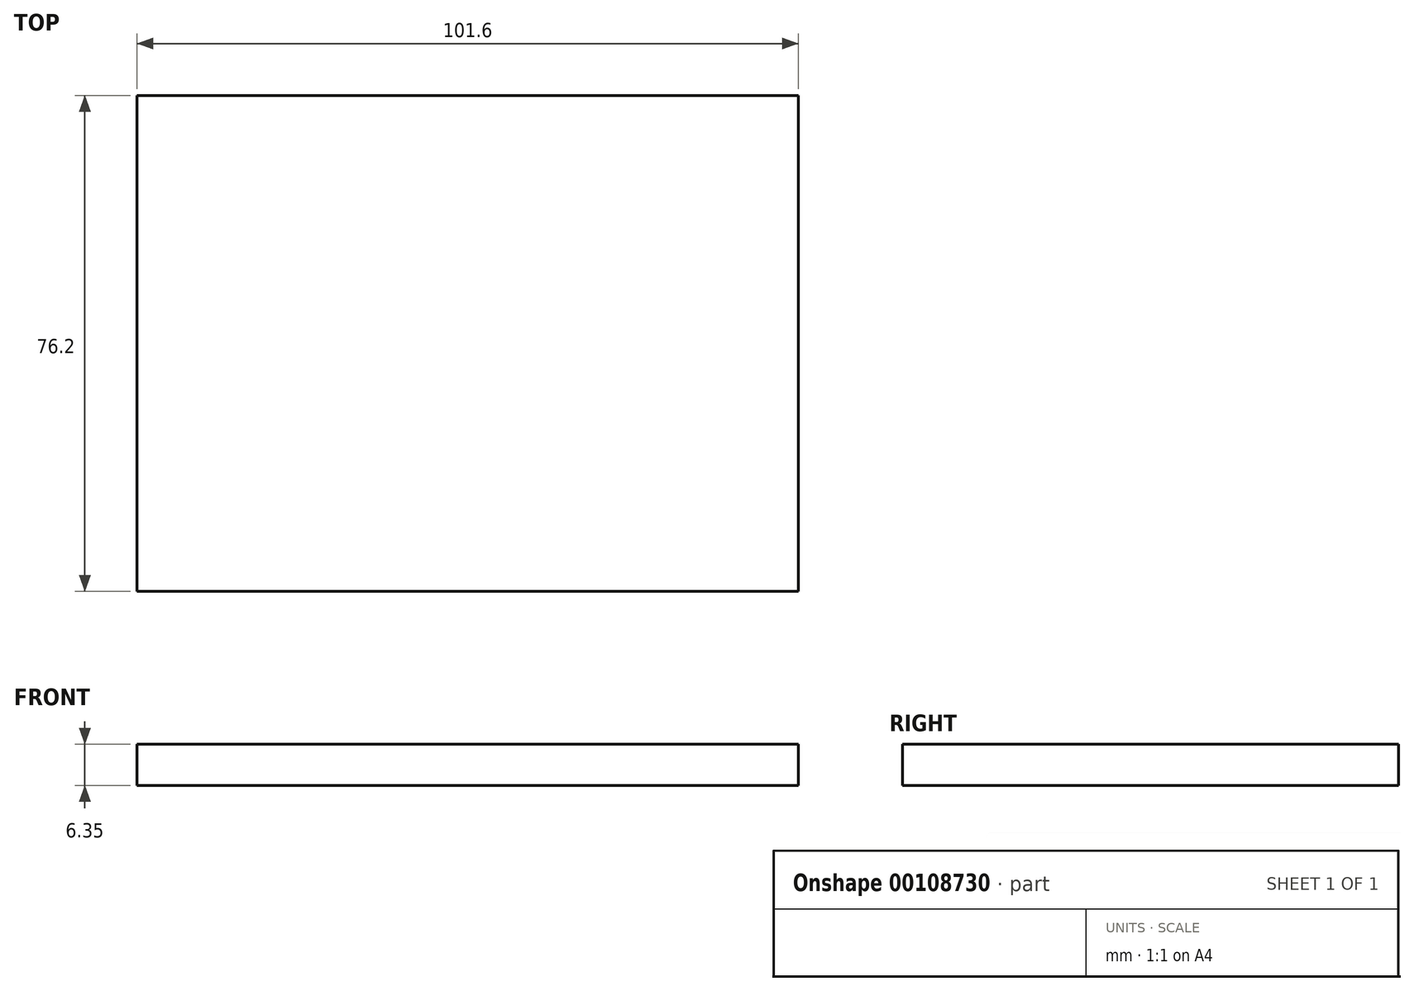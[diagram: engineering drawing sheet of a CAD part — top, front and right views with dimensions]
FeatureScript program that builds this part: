
annotation { "Feature Type Name" : "Feature", "Feature Type Description" : "" }
export const myFeature = defineFeature(function(context is Context, id is Id, definition is map)
    precondition{}
    {
        {
            var Q0;
            Q0=qCreatedBy(makeId("Top.planeOp"),FACE);
            var sketch = newSketch(context, id + "F0", { "sketchPlane" : qUnion([Q0])});
            skLineSegment(sketch, "E0.bottom", {"start": v(50.8, 38.1) * mm, "end": v(-50.8, 38.1) * mm});
            skLineSegment(sketch, "E0.top", {"start": v(50.8, -38.1) * mm, "end": v(-50.8, -38.1) * mm});
            skLineSegment(sketch, "E0.left", {"start": v(50.8, 38.1) * mm, "end": v(50.8, -38.1) * mm});
            skLineSegment(sketch, "E0.right", {"start": v(-50.8, 38.1) * mm, "end": v(-50.8, -38.1) * mm});
            skPoint(sketch, "E0.middle", {"position": v(0, 0) * mm});
            skSolve(sketch);
        }
        {
            var Q0;
            Q0=makeQuery(id+"F0.imprint","IMPRINT",FACE,{"disambiguationData":[TD([[makeQuery(id+"F0.imprint","IMPRINT",EDGE,{"derivedFrom":sQuery(id+"F0.wireOp",EDGE,"E0.bottom")}),1.0]])]});
            extrude(context, id + "F1", {"entities" : qUnion([Q0]), "depth" : 6.35 * mm});
        }
    });
